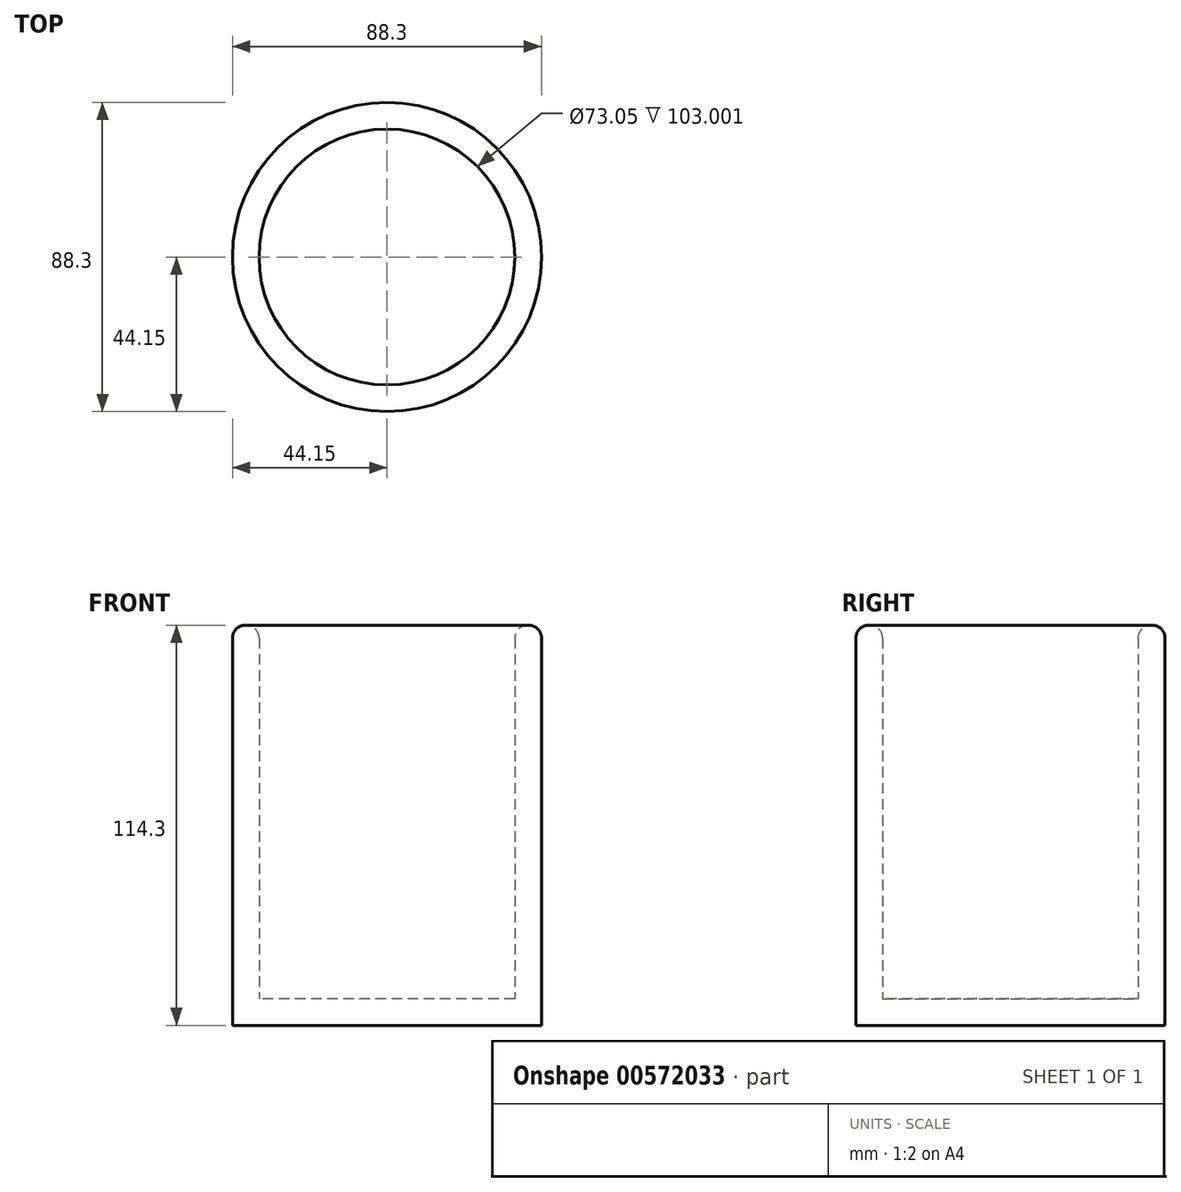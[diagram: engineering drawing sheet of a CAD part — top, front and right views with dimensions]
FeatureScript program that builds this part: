
annotation { "Feature Type Name" : "Feature", "Feature Type Description" : "" }
export const myFeature = defineFeature(function(context is Context, id is Id, definition is map)
    precondition{}
    {
        {
            var Q0;
            Q0=qCreatedBy(makeId("Top.planeOp"),FACE);
            var sketch = newSketch(context, id + "F0", { "sketchPlane" : qUnion([Q0])});
            skCircle(sketch, "E0", {"center": v(0, 0) * mm, "radius": 44.15 * mm});
            skSolve(sketch);
        }
        {
            var Q0;
            Q0 = qSketchRegion(id + "F0", true);
            extrude(context, id + "F1", {"entities" : qUnion([Q0]), "depth" : 114.3 * mm, "offsetDistance" : 25.4 * mm});
        }
        {
            var Q0;
            Q0=makeQuery(id+"F1.opExtrude","CAP_FACE",FACE,{"disambiguationData":[OSD([sQuery(id+"F0.wireOp",EDGE,"E0")])],"isStart":false});
            shell(context, id + "F2", {"entities" : qUnion([Q0]), "thickness" : 7.62 * mm});
        }
        {
            var Q0;
            Q0=makeQuery(id+"F1.opExtrude","CAP_FACE",FACE,{"disambiguationData":[OSD([sQuery(id+"F0.wireOp",EDGE,"E0")])],"isStart":false});
            var Q1;
            Q1=makeQuery(id+"F1.opExtrude","CAP_EDGE",EDGE,{"disambiguationData":[OSD([sQuery(id+"F0.wireOp",EDGE,"E0")])],"isStart":false});
            fillet(context, id + "F3", {"entities" : qUnion([Q0, Q1]), "radius" : 3.68 * mm, "tangentPropagation" : true, "allowEdgeOverflow" : false});
        }
    });
